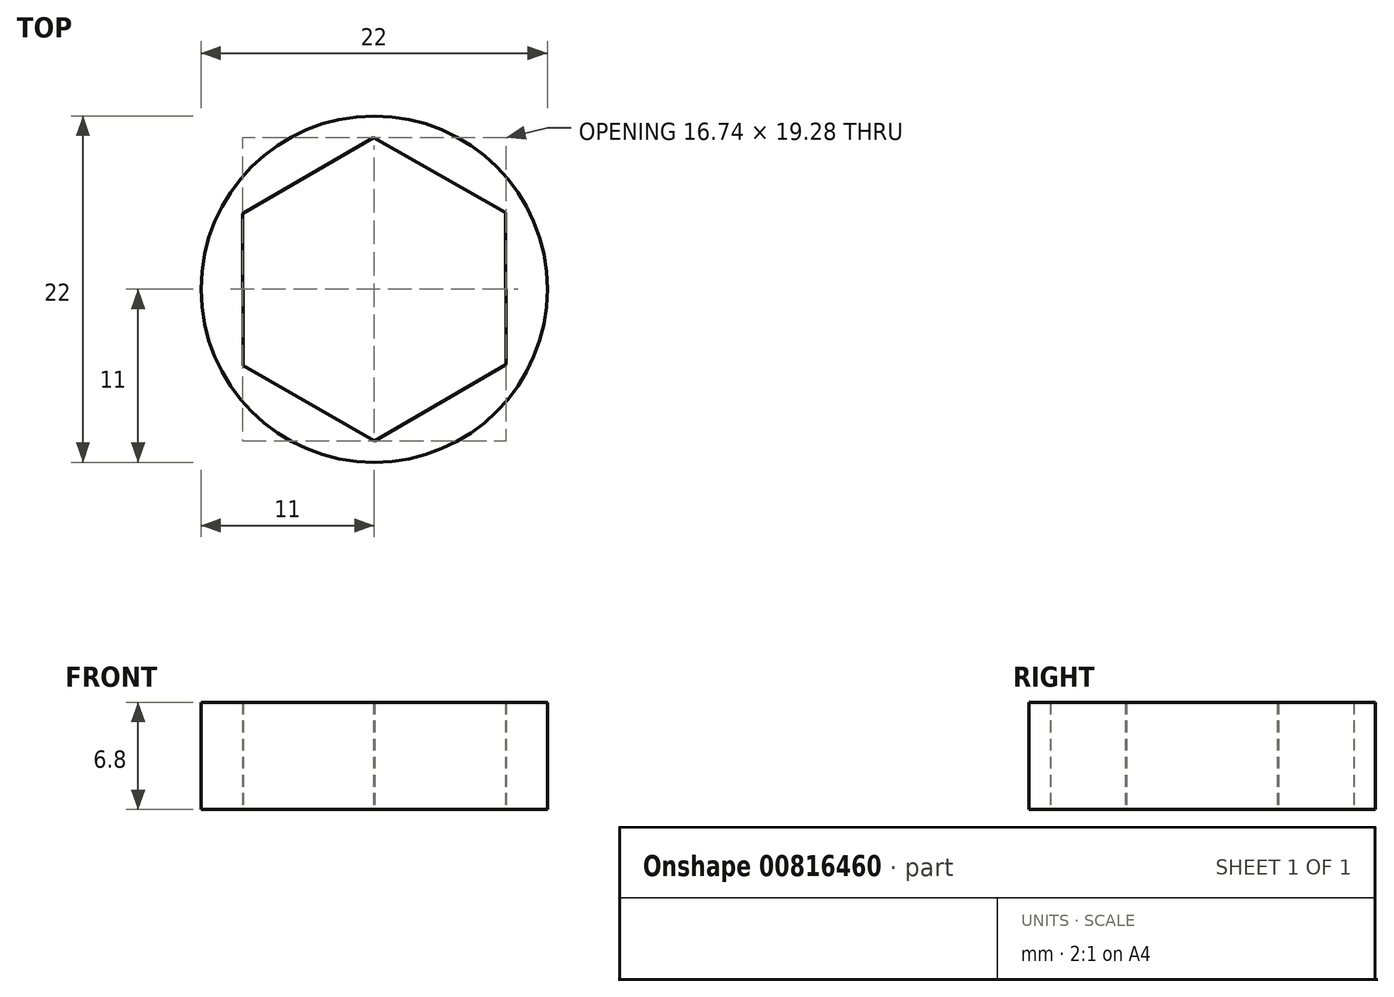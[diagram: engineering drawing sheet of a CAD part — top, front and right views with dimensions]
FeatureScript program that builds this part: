
annotation { "Feature Type Name" : "Feature", "Feature Type Description" : "" }
export const myFeature = defineFeature(function(context is Context, id is Id, definition is map)
    precondition{}
    {
        {
            var Q0;
            Q0=qCreatedBy(makeId("Top.planeOp"),FACE);
            var sketch = newSketch(context, id + "F0", { "sketchPlane" : qUnion([Q0])});
            skCircle(sketch, "E0", {"center": v(0, 0) * mm, "radius": 11 * mm});
            skCircle(sketch, "E1.cCircle", {"center": v(0, 0) * mm, "radius": 8.35 * mm, "construction": true});
            skLineSegment(sketch, "E1.0", {"start": v(-0.04, 9.64) * mm, "end": v(8.33, 4.85) * mm});
            skLineSegment(sketch, "E1.1", {"start": v(8.33, 4.85) * mm, "end": v(8.37, -4.79) * mm});
            skLineSegment(sketch, "E1.2", {"start": v(8.37, -4.79) * mm, "end": v(0.04, -9.64) * mm});
            skLineSegment(sketch, "E1.3", {"start": v(0.04, -9.64) * mm, "end": v(-8.33, -4.85) * mm});
            skLineSegment(sketch, "E1.4", {"start": v(-8.33, -4.85) * mm, "end": v(-8.37, 4.79) * mm});
            skLineSegment(sketch, "E1.5", {"start": v(-8.37, 4.79) * mm, "end": v(-0.04, 9.64) * mm});
            skPoint(sketch, "E1.0.midPoint", {"position": v(4.15, 7.25) * mm});
            skSolve(sketch);
        }
        {
            var Q0;
            Q0=makeQuery(id+"F0.imprint","IMPRINT",FACE,{"disambiguationData":[TD([[makeQuery(id+"F0.imprint","IMPRINT",EDGE,{"derivedFrom":sQuery(id+"F0.wireOp",EDGE,"E0")}),1.0]])]});
            extrude(context, id + "F1", {"entities" : qUnion([Q0]), "depth" : 6.8 * mm, "offsetDistance" : 25 * mm});
        }
    });
